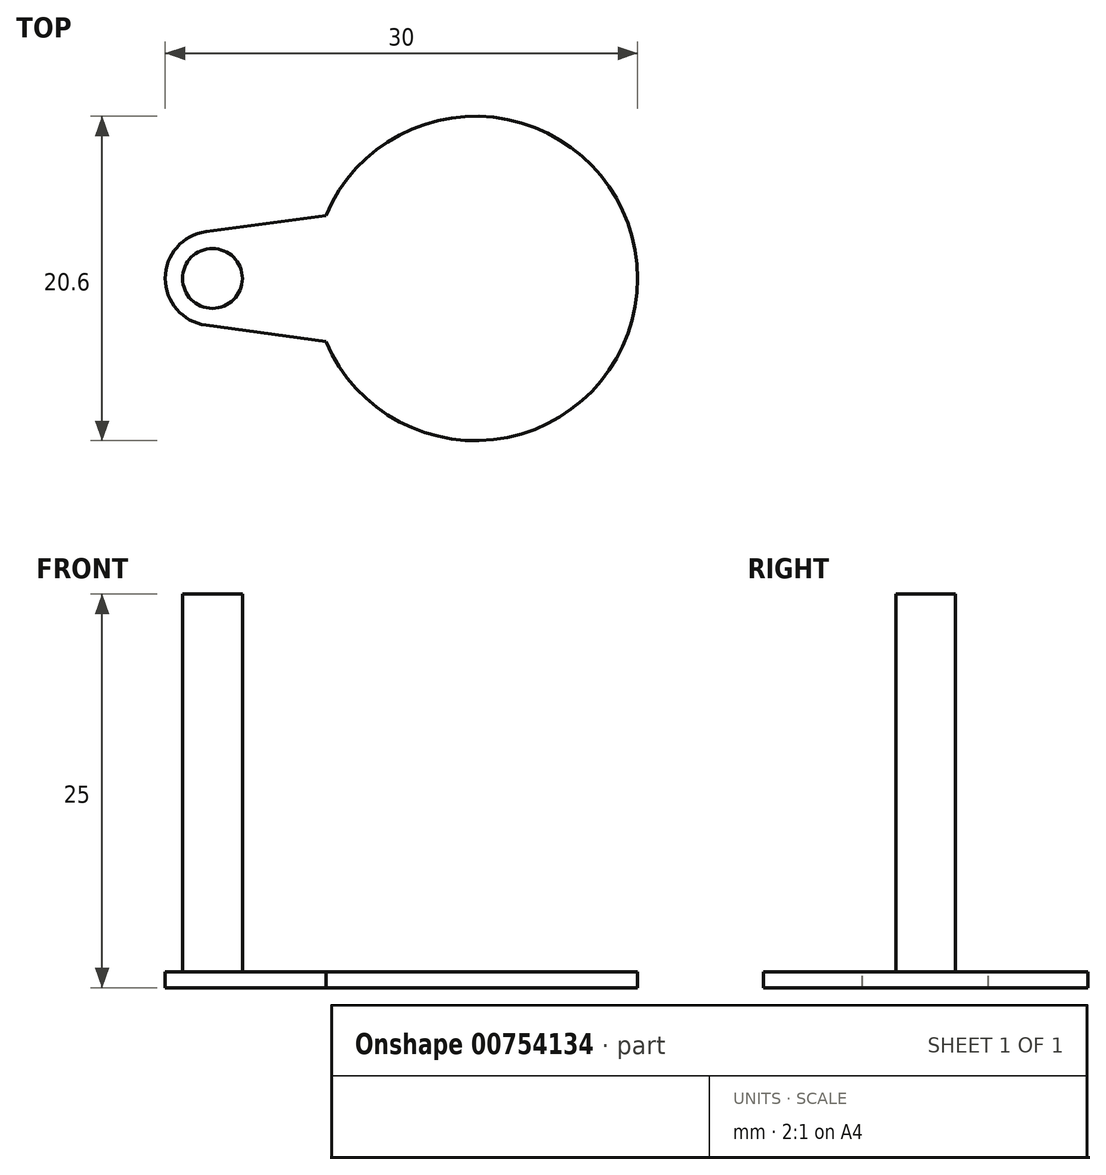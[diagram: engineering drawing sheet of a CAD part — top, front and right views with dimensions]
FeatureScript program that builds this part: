
annotation { "Feature Type Name" : "Feature", "Feature Type Description" : "" }
export const myFeature = defineFeature(function(context is Context, id is Id, definition is map)
    precondition{}
    {
        {
            var Q0;
            Q0=qCreatedBy(makeId("Top.planeOp"),FACE);
            var sketch = newSketch(context, id + "F0", { "sketchPlane" : qUnion([Q0])});
            skCircle(sketch, "E0", {"center": v(0, 0) * mm, "radius": 10.3 * mm});
            skCircle(sketch, "E1", {"center": v(-16.7, 0) * mm, "radius": 1.5 * mm});
            skCircle(sketch, "E2", {"center": v(-16.7, 0) * mm, "radius": 3 * mm});
            skPoint(sketch, "E3", {"position": v(-19.7, 0) * mm});
            skPoint(sketch, "E4", {"position": v(10.3, 0) * mm});
            skLineSegment(sketch, "E5", {"start": v(-17.1, -2.97) * mm, "end": v(-9.5, -4) * mm});
            skLineSegment(sketch, "E6", {"start": v(-17.1, 2.97) * mm, "end": v(-9.5, 4) * mm});
            skLineSegment(sketch, "E7", {"start": v(-9.5, 4) * mm, "end": v(-9.5, -4) * mm, "construction": true});
            skSolve(sketch);
        }
        {
            var Q0;
            {var subQ0=sQuery(id+"F0.wireOp",EDGE,"E0");var subQ1=makeQuery(id+"F0.imprint","INTERSECT",VERTEX,{"derivedFrom":[subQ0,sQuery(id+"F0.wireOp",EDGE,"E5")]});Q0=makeQuery(id+"F0.imprint","IMPRINT",FACE,{"disambiguationData":[TD([[makeQuery(id+"F0.imprint","IMPRINT",EDGE,{"disambiguationData":[TD([[subQ1,1.0]])],"derivedFrom":subQ0}),1.0]])]});}
            var Q1;
            {var subQ0=sQuery(id+"F0.wireOp",EDGE,"E5");Q1=makeQuery(id+"F0.imprint","IMPRINT",FACE,{"disambiguationData":[TD([[makeQuery(id+"F0.imprint","IMPRINT",EDGE,{"derivedFrom":subQ0}),1.0]])]});}
            var Q2;
            Q2=makeQuery(id+"F0.imprint","IMPRINT",FACE,{"disambiguationData":[TD([[makeQuery(id+"F0.imprint","IMPRINT",EDGE,{"derivedFrom":sQuery(id+"F0.wireOp",EDGE,"E1")}),-1.0]])]});
            extrude(context, id + "F1", {"entities" : qUnion([Q0, Q1, Q2]), "oppositeDirection" : true, "depth" : 1 * mm, "offsetDistance" : 25 * mm});
        }
        {
            var Q0;
            Q0=makeQuery(id+"F1.opExtrude","CAP_FACE",FACE,{"disambiguationData":[OSD([sQuery(id+"F0.wireOp",EDGE,"E0"),sQuery(id+"F0.wireOp",EDGE,"E1"),sQuery(id+"F0.wireOp",EDGE,"E2"),sQuery(id+"F0.wireOp",EDGE,"E5"),sQuery(id+"F0.wireOp",EDGE,"E6")])],"isStart":false});
            var sketch = newSketch(context, id + "F2", { "sketchPlane" : qUnion([Q0])});
            skCircle(sketch, "E8", {"center": v(-16.7, 0) * mm, "radius": 1.9 * mm});
            skSolve(sketch);
        }
        {
            var Q0;
            Q0 = qSketchRegion(id + "F2", true);
            extrude(context, id + "F3", {"entities" : qUnion([Q0]), "operationType" : NewBodyOperationType.ADD, "oppositeDirection" : true, "depth" : 25 * mm, "offsetDistance" : 25 * mm});
        }
    });
